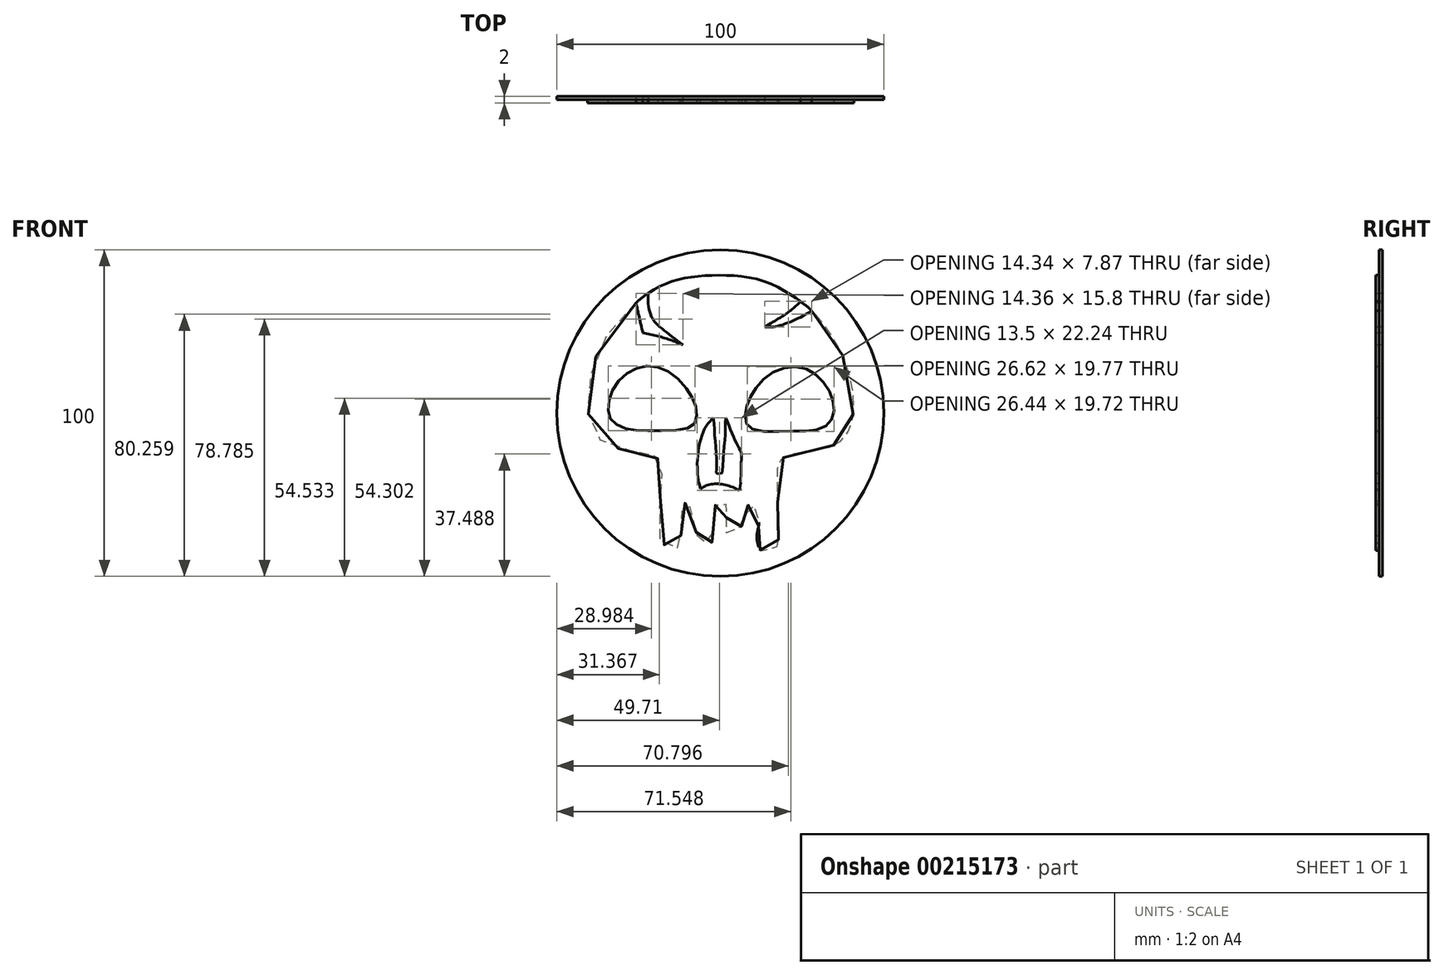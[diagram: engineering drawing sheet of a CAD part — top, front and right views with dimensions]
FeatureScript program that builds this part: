
annotation { "Feature Type Name" : "Feature", "Feature Type Description" : "" }
export const myFeature = defineFeature(function(context is Context, id is Id, definition is map)
    precondition{}
    {
        {
            var Q0;
            Q0=qCreatedBy(makeId("Front.planeOp"),FACE);
            var sketch = newSketch(context, id + "F0", { "sketchPlane" : qUnion([Q0])});
            skSolve(sketch);
        }
        {
            var Q0;
            Q0=qCreatedBy(makeId("Front.planeOp"),FACE);
            var sketch = newSketch(context, id + "F1", { "sketchPlane" : qUnion([Q0])});
            skFitSpline(sketch, "E0", {"points": [v(0, 42.21) * mm, v(-11.72, 41.16) * mm, v(-21.43, 37.1) * mm, v(-30.9, 28.7) * mm, v(-37.63, 18.55) * mm, v(-40.34, 7.41) * mm, v(-40.46, 0) * mm, v(-38.7, -6.08) * mm, v(-33.24, -10.3) * mm, v(-27.66, -11.36) * mm, v(-22.63, -12.3) * mm, v(-19.43, -13.56) * mm, v(-17.47, -17.28) * mm, v(-17.89, -18.61) * mm, v(-18.37, -24.15) * mm, v(-18.87, -33.53) * mm, v(-18.37, -39.08) * mm, v(-15.65, -41.04) * mm, v(-13.56, -41.23) * mm, v(-12.56, -41.1) * mm, v(-12.24, -39.83) * mm, v(-11.98, -36.56) * mm, v(-12.24, -33.56) * mm, v(-12.4, -32.36) * mm, v(-11.05, -28.18) * mm, v(-10.45, -26.99) * mm, v(-9.7, -27.44) * mm, v(-8.96, -31.02) * mm, v(-7.32, -36.7) * mm, v(-6.87, -39.23) * mm, v(-6.65, -39.73) * mm, v(-5.23, -39.68) * mm, v(-3.29, -39.68) * mm, v(-2.53, -39.55) * mm, v(-2.4, -38.04) * mm, v(-2.24, -35.2) * mm, v(-1.5, -28.63) * mm, v(-1.5, -27.73) * mm, v(-0.52, -27.73) * mm, v(0.82, -27.77) * mm, v(1.64, -27.85) * mm, v(1.83, -28.82) * mm, v(1.83, -36.32) * mm, v(1.83, -37.22) * mm, v(2.2, -37.51) * mm, v(4.52, -35.98) * mm, v(7.76, -33.74) * mm, v(8.03, -33.07) * mm, v(7.95, -31.4) * mm, v(7.76, -28.4) * mm, v(8.06, -28.18) * mm, v(10, -28.1) * mm, v(10.49, -28.48) * mm, v(10.71, -29.34) * mm, v(11.72, -32.18) * mm, v(11.65, -35.01) * mm, v(11.19, -37.22) * mm, v(11.34, -39.35) * mm, v(11.66, -40.83) * mm, v(11.88, -41.68) * mm, v(12.54, -42.05) * mm, v(14.48, -41.68) * mm, v(16.62, -41.17) * mm, v(17.3, -40.96) * mm, v(17.7, -39.33) * mm, v(18.08, -36.87) * mm, v(17.9, -33.23) * mm, v(17.56, -29.62) * mm, v(17.53, -20.49) * mm, v(17.69, -15.86) * mm, v(19.63, -13.4) * mm, v(27.92, -11.46) * mm, v(34.41, -9.97) * mm, v(38, -7.5) * mm, v(40, -3.47) * mm, v(40.68, -0.56) * mm, v(40.68, 5.93) * mm, v(37.22, 18.07) * mm, v(31.73, 27.06) * mm, v(28.14, 31.23) * mm, v(24.25, 34.4) * mm, v(13.7, 40.27) * mm, v(0, 42.21) * mm]});
            skFitSpline(sketch, "E1", {"points": [v(-25.81, 33.77) * mm, v(-23.7, 24.61) * mm], "startDerivative": vector(2.09, -9.14) * mm, "endDerivative": vector(2.09, -9.14) * mm});
            skFitSpline(sketch, "E2", {"points": [v(-23.7, 24.61) * mm, v(-16.96, 22.97) * mm, v(-11.45, 20.89) * mm], "startDerivative": vector(13.34, -2.84) * mm, "endDerivative": vector(11.13, -4.64) * mm});
            skFitSpline(sketch, "E3", {"points": [v(-11.45, 20.89) * mm, v(-16.96, 25.15) * mm, v(-20.29, 28.25) * mm, v(-21.93, 32.47) * mm, v(-22.05, 36.69) * mm], "startDerivative": vector(-19.63, 15.23) * mm, "endDerivative": vector(0.8, 18.17) * mm});
            skFitSpline(sketch, "E4", {"points": [v(24.54, 34.2) * mm, v(20.63, 30.76) * mm, v(13.63, 26.4) * mm], "startDerivative": vector(-7.1, -7.92) * mm, "endDerivative": vector(-14.38, -8.75) * mm});
            skFitSpline(sketch, "E5", {"points": [v(13.63, 26.4) * mm, v(17.28, 26.57) * mm, v(24.65, 29.42) * mm, v(27.97, 31.4) * mm], "startDerivative": vector(13.04, -1.16) * mm, "endDerivative": vector(9.37, 6.14) * mm});
            skFitSpline(sketch, "E6", {"points": [v(-22.52, 14.42) * mm, v(-15.86, 12.73) * mm, v(-9.82, 6.87) * mm, v(-7.42, 1.72) * mm, v(-7.6, -2.72) * mm, v(-10.97, -4.85) * mm, v(-21.37, -5.34) * mm, v(-28.55, -4.85) * mm, v(-33, -2.45) * mm, v(-34.32, 1.28) * mm, v(-32.9, 7.14) * mm, v(-28.46, 12.2) * mm, v(-22.52, 14.42) * mm]});
            skFitSpline(sketch, "E7.MirrorC", {"points": [v(23.03, 14.16) * mm, v(15.87, 12.34) * mm, v(10.54, 7.13) * mm, v(8.09, 2.17) * mm, v(7.77, -2.53) * mm, v(10.22, -5.05) * mm, v(21.02, -5.55) * mm, v(28.93, -5.23) * mm, v(33.45, -2.91) * mm, v(34.77, 1.48) * mm, v(33.26, 6.88) * mm, v(28.93, 12.03) * mm, v(23.03, 14.16) * mm]});
            skFitSpline(sketch, "E8", {"points": [v(-2.1, -1.4) * mm, v(-4.89, -4.97) * mm, v(-6.96, -13.76) * mm, v(-6.7, -20.35) * mm, v(-6.08, -23.11) * mm], "startDerivative": vector(-12.66, -12.53) * mm, "endDerivative": vector(3.72, -13.83) * mm});
            skFitSpline(sketch, "E9", {"points": [v(-6.08, -23.11) * mm, v(-3.58, -21.94) * mm, v(-0.59, -21.68) * mm, v(2.8, -22.3) * mm, v(5.69, -23.63) * mm], "startDerivative": vector(10.12, 5.73) * mm, "endDerivative": vector(9.93, -5.43) * mm});
            skFitSpline(sketch, "E10", {"points": [v(5.69, -23.63) * mm, v(6.2, -21.26) * mm, v(6.43, -15.07) * mm, v(6.43, -12.27) * mm, v(5.69, -10.63) * mm, v(4.08, -7.34) * mm, v(1.63, -1.42) * mm], "startDerivative": vector(7.54, 13.44) * mm, "endDerivative": vector(-11.31, 26.08) * mm});
            skFitSpline(sketch, "E11", {"points": [v(1.63, -1.42) * mm, v(1.5, -6.3) * mm, v(0.97, -12.47) * mm, v(0.62, -17.8) * mm, v(0.4, -18.42) * mm, v(-0.53, -18.51) * mm, v(-1.11, -18.42) * mm, v(-1.16, -17.31) * mm, v(-1.25, -12.56) * mm, v(-1.69, -6.97) * mm, v(-2.1, -1.4) * mm], "startDerivative": vector(-3.41, -34.26) * mm, "endDerivative": vector(-4.32, 40.08) * mm});
            skCircle(sketch, "E12", {"center": v(0, 0) * mm, "radius": 50 * mm});
            skSolve(sketch);
        }
        {
            var Q0;
            Q0=makeQuery(id+"F1.imprint","IMPRINT",FACE,{"disambiguationData":[TD([[makeQuery(id+"F1.imprint","IMPRINT",EDGE,{"derivedFrom":sQuery(id+"F1.wireOp",EDGE,"E0")}),-1.0]])]});
            var Q1;
            Q1=makeQuery(id+"F1.imprint","IMPRINT",FACE,{"disambiguationData":[TD([[makeQuery(id+"F1.imprint","IMPRINT",EDGE,{"derivedFrom":sQuery(id+"F1.wireOp",EDGE,"E0")}),1.0]])]});
            var Q2;
            Q2=makeQuery(id+"F1.imprint","IMPRINT",FACE,{"disambiguationData":[TD([[makeQuery(id+"F1.imprint","IMPRINT",EDGE,{"derivedFrom":sQuery(id+"F1.wireOp",EDGE,"E6")}),-1.0]])]});
            var Q3;
            Q3=makeQuery(id+"F1.imprint","IMPRINT",FACE,{"disambiguationData":[TD([[makeQuery(id+"F1.imprint","IMPRINT",EDGE,{"derivedFrom":sQuery(id+"F1.wireOp",EDGE,"E7.MirrorC")}),1.0]])]});
            var Q4;
            Q4=makeQuery(id+"F1.imprint","IMPRINT",FACE,{"disambiguationData":[TD([[makeQuery(id+"F1.imprint","IMPRINT",EDGE,{"derivedFrom":sQuery(id+"F1.wireOp",EDGE,"E8")}),1.0]])]});
            extrude(context, id + "F2", {"entities" : qUnion([Q0, Q1, Q2, Q3, Q4]), "oppositeDirection" : true, "depth" : 1 * mm, "offsetDistance" : 25 * mm});
        }
        {
            var Q0;
            Q0=makeQuery(id+"F1.imprint","IMPRINT",FACE,{"disambiguationData":[TD([[makeQuery(id+"F1.imprint","IMPRINT",EDGE,{"derivedFrom":sQuery(id+"F1.wireOp",EDGE,"E0")}),1.0]])]});
            extrude(context, id + "F3", {"entities" : qUnion([Q0]), "depth" : 1 * mm, "offsetDistance" : 25 * mm});
        }
        {
            var Q0;
            Q0=makeQuery(id+"F2.opExtrude","SWEPT_BODY",BODY,{"disambiguationData":[OSD([sQuery(id+"F1.wireOp",EDGE,"E12")])]});
            var Q1;
            Q1=qCreatedBy(makeId("Origin.pointOp"),VERTEX);
            transform(context, id + "F4", {"entities" : qUnion([Q0]), "transformType" : TransformType.SCALE_UNIFORMLY, "scale" : 1, "scalePoint" : qUnion([Q1]), "makeCopy" : false});
        }
    });
